# Revit family: QF_ELECTROLUXPROFESSIONAL_1LSNA1_WE1100P_E
name_source: partatom
category: Attrezzature speciali
units: mm (PartAtom-declared; Revit-internal decimal feet)

## family parameters
Basato su piano di lavoro = No
Condiviso = No
Punto di calcolo locali = No
Quota connettore circolare = Usa diametro
Sempre verticale = Sì
Taglio con vuoti quando caricato = No
Tipo di parte = Normale

## types (4) — shared parameters
Depth = 822 mm
Height = 850 mm  [stored 2.78871 ft]
Latent Heat Output = 0.0
Modello = WE1100P
Phase = 1
Produttore = Electrolux Professional
Sensible Heat Output = 0.0
URL = www.electroluxprofessional.com
Volts = 240 V
Watts = 2000 W
Width = 686 mm  [stored 2.25066 ft]
zero-valued in all types: Gas KW, Prospetto di default, Steam Pounds per Hour

## per-type parameters (varying)
| type | Cycle | Depth Actual | Descrizione | Height Actual | Item Number | Length Actual | Weight |
| 988690005 | 60 Hz | 0 mm  [stored 0 ft] | myPRO XL SMART PROFESSIONAL WASHER WE1100P PUMP 208-240/60/1N 2,0KW SYMBOLS EU SST/DARK BLUE | 0 mm  [stored 0 ft] | 1L0H20 | 0 mm  [stored 0 ft] | 0 |
| 988690004 | 50 Hz | 765 mm  [stored 2.50984 ft] | myPRO XL SMART PROFESSIONAL WASHER WE1100P 12KG PUMP 220-240/50/1N 2,0KW SYMBOLS UK SST/DARK BLUE | 1098 mm  [stored 3.60236 ft] | 1L0GJV | 686 mm  [stored 2.25066 ft] | 136 |
| 988690006 | 50 Hz | 765 mm  [stored 2.50984 ft] | myPRO XL SMART PROFESSIONAL WASHER WE1100P 12KG PUMP 220-240/50/1N 2,0KW SYMBOLS EU SST/DARK BLUE | 1098 mm  [stored 3.60236 ft] | 1L0GM8 | 686 mm  [stored 2.25066 ft] | 136 |
| 988690003 | 50 Hz | 765 mm  [stored 2.50984 ft] | myPRO XL SMART PROFESSIONAL WASHER WE1100P 12KG PUMP 220-240/50/1N 2,0KW SYMBOLS EU SST/DARK BLUE | 1098 mm  [stored 3.60236 ft] | 1L0GJU | 686 mm  [stored 2.25066 ft] | 136 |

note: [stored X ft] marks values corroborated as IEEE doubles in the binary element streams (Revit-internal decimal feet)

## geometry (parser evidence)
native form markers: Sweep x2
no freeform markers — native parametric forms only
